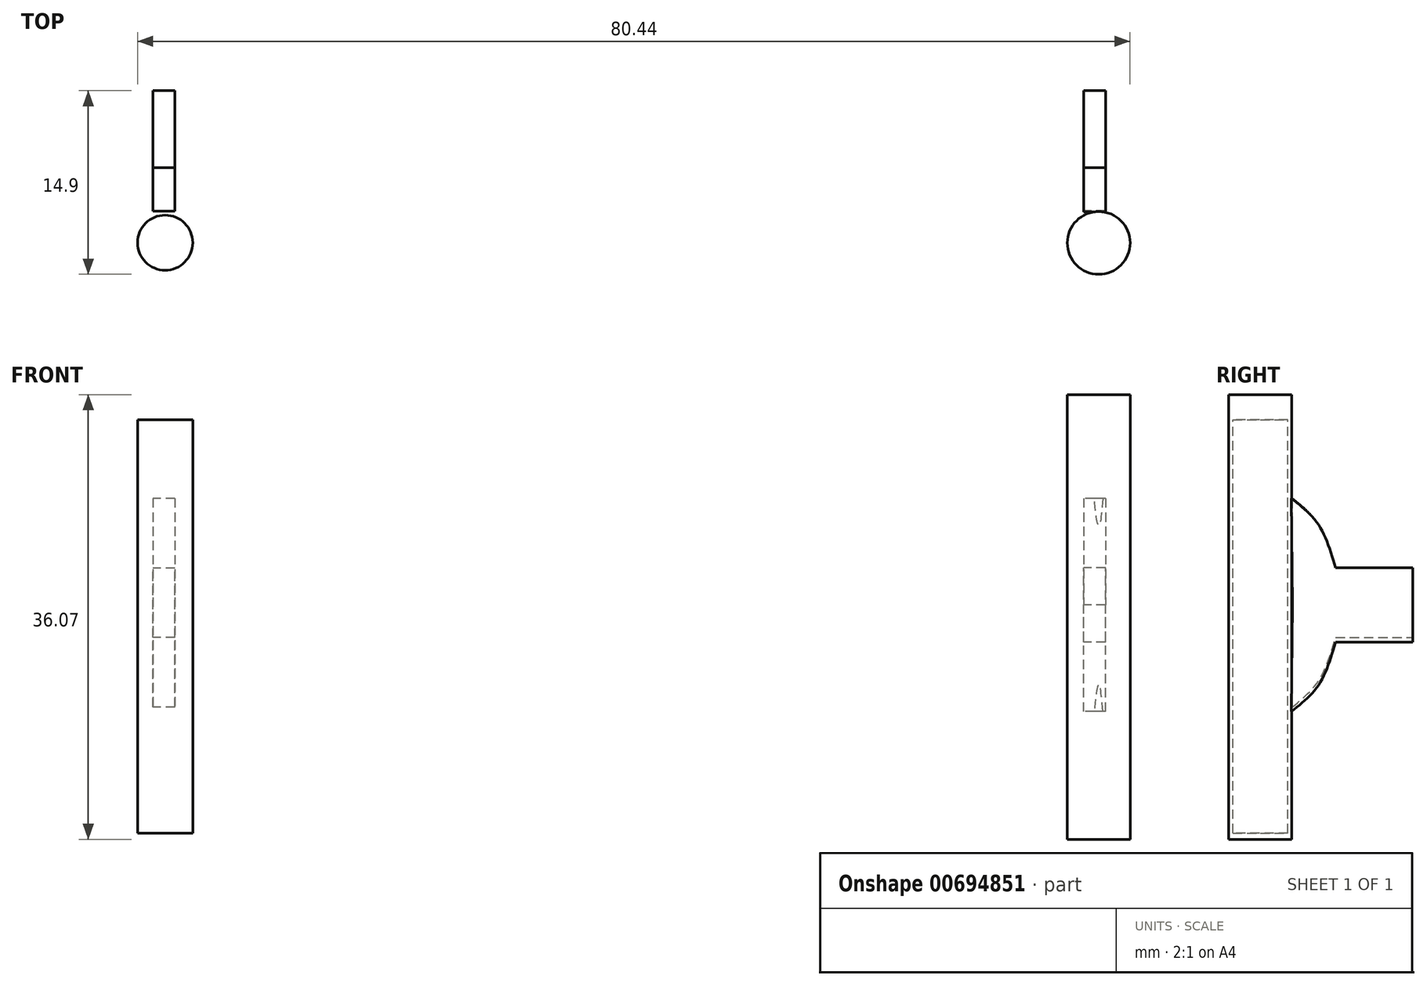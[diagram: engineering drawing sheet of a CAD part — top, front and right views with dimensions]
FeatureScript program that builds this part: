
annotation { "Feature Type Name" : "Feature", "Feature Type Description" : "" }
export const myFeature = defineFeature(function(context is Context, id is Id, definition is map)
    precondition{}
    {
        {
            var Q0;
            Q0=qCreatedBy(makeId("Top.planeOp"),FACE);
            var sketch = newSketch(context, id + "F0", { "sketchPlane" : qUnion([Q0])});
            skLineSegment(sketch, "E0", {"start": v(-51.87, 6.38) * mm, "end": v(46.37, 6.38) * mm});
            skFitSpline(sketch, "E1", {"points": [v(46.37, 6.38) * mm, v(69.04, 11.27) * mm, v(78.15, 20.83) * mm, v(81.04, 14.83) * mm, v(70.82, 4.6) * mm, v(46.37, 0) * mm, v(0, 0) * mm, v(-50.76, 0) * mm, v(-72.1, 6.38) * mm, v(-78.31, 11.94) * mm, v(-78.1, 18.16) * mm, v(-68.54, 12.16) * mm, v(-51.87, 6.38) * mm], "startDerivative": vector(273.4, 3.83) * mm, "endDerivative": vector(210.6, -44.02) * mm});
            skSolve(sketch);
        }
        {
            var Q0;
            Q0=sQuery(id+"F0.wireOp",EDGE,"E0");
            var Q1;
            Q1=sQuery(id+"F0.wireOp",EDGE,"E1");
            extrude(context, id + "F1", {"bodyType" : ToolBodyType.SURFACE, "surfaceEntities" : qUnion([Q0, Q1]), "depth" : 42.42 * mm, "offsetDistance" : 25.4 * mm});
        }
        {
            var Q0;
            Q0=qCreatedBy(makeId("Right.planeOp"),FACE);
            cPlane(context, id + "F2", {"entities" : qUnion([Q0]), "cplaneType" : CPlaneType.OFFSET, "offset" : 37.6 * mm, "oppositeDirection" : true, "width" : 152.4 * mm, "height" : 152.4 * mm});
        }
        {
            var Q0;
            Q0=qCreatedBy(makeId("Right.planeOp"),FACE);
            cPlane(context, id + "F3", {"entities" : qUnion([Q0]), "cplaneType" : CPlaneType.OFFSET, "offset" : 33.27 * mm, "width" : 152.4 * mm, "height" : 152.4 * mm});
        }
        {
            var Q0;
            Q0=qCreatedBy(makeId("Top.planeOp"),FACE);
            cPlane(context, id + "F4", {"entities" : qUnion([Q0]), "cplaneType" : CPlaneType.OFFSET, "offset" : 32 * mm, "width" : 152.4 * mm, "height" : 152.4 * mm});
        }
        {
            var Q0;
            Q0=qCreatedBy(id+"F4.planeOp",FACE);
            var sketch = newSketch(context, id + "F5", { "sketchPlane" : qUnion([Q0])});
            skCircle(sketch, "E2", {"center": v(-32.8, -12.56) * mm, "radius": 5.12 * mm});
            skCircle(sketch, "E3", {"center": v(39.44, -12.56) * mm, "radius": 5.34 * mm});
            skSolve(sketch);
        }
        {
            var Q0;
            Q0=sQuery(id+"F5.wireOp",EDGE,"E2");
            extrude(context, id + "F6", {"bodyType" : ToolBodyType.SURFACE, "surfaceEntities" : qUnion([Q0]), "depth" : 5.6 * mm, "offsetDistance" : 25.4 * mm});
        }
        {
            var Q0;
            Q0=qCreatedBy(id+"F4.planeOp",FACE);
            var sketch = newSketch(context, id + "F7", { "sketchPlane" : qUnion([Q0])});
            skCircle(sketch, "E4", {"center": v(42.77, -12.33) * mm, "radius": 5.23 * mm});
            skSolve(sketch);
        }
        {
            var Q0;
            Q0=sQuery(id+"F7.wireOp",EDGE,"E4");
            extrude(context, id + "F8", {"bodyType" : ToolBodyType.SURFACE, "surfaceEntities" : qUnion([Q0]), "depth" : 5.6 * mm, "offsetDistance" : 25.4 * mm});
        }
        {
            var Q0;
            Q0=qCreatedBy(makeId("Top.planeOp"),FACE);
            var sketch = newSketch(context, id + "F9", { "sketchPlane" : qUnion([Q0])});
            skCircle(sketch, "E5", {"center": v(-32.8, -12.56) * mm, "radius": 5.25 * mm});
            skCircle(sketch, "E6", {"center": v(43, -12.11) * mm, "radius": 5.28 * mm});
            skSolve(sketch);
        }
        {
            var Q0;
            Q0=sQuery(id+"F9.wireOp",EDGE,"E5");
            extrude(context, id + "F10", {"bodyType" : ToolBodyType.SURFACE, "surfaceEntities" : qUnion([Q0]), "depth" : 5.33 * mm, "offsetDistance" : 25.4 * mm});
        }
        {
            var Q0;
            Q0=qCreatedBy(makeId("Top.planeOp"),FACE);
            var sketch = newSketch(context, id + "F11", { "sketchPlane" : qUnion([Q0])});
            skCircle(sketch, "E7", {"center": v(43, -12.33) * mm, "radius": 5.35 * mm});
            skSolve(sketch);
        }
        {
            var Q0;
            Q0=sQuery(id+"F11.wireOp",EDGE,"E7");
            extrude(context, id + "F12", {"bodyType" : ToolBodyType.SURFACE, "surfaceEntities" : qUnion([Q0]), "depth" : 5.6 * mm, "offsetDistance" : 25.4 * mm});
        }
        {
            var Q0;
            Q0=qCreatedBy(makeId("Front.planeOp"),FACE);
            cPlane(context, id + "F13", {"entities" : qUnion([Q0]), "cplaneType" : CPlaneType.OFFSET, "offset" : 11.94 * mm, "width" : 152.4 * mm, "height" : 152.4 * mm});
        }
        {
            var Q0;
            Q0=qCreatedBy(id+"F4.planeOp",FACE);
            cPlane(context, id + "F14", {"entities" : qUnion([Q0]), "cplaneType" : CPlaneType.OFFSET, "offset" : 2.03 * mm, "width" : 152.4 * mm, "height" : 152.4 * mm});
        }
        {
            var Q0;
            Q0=qCreatedBy(id+"F14.planeOp",FACE);
            var sketch = newSketch(context, id + "F15", { "sketchPlane" : qUnion([Q0])});
            skCircle(sketch, "E8", {"center": v(-32.8, -12.33) * mm, "radius": 2.23 * mm});
            skSolve(sketch);
        }
        {
            var Q0;
            Q0 = qSketchRegion(id + "F15", true);
            extrude(context, id + "F16", {"entities" : qUnion([Q0]), "oppositeDirection" : true, "depth" : 33.53 * mm, "offsetDistance" : 25.4 * mm});
        }
        {
            var Q0;
            Q0=qCreatedBy(makeId("Top.planeOp"),FACE);
            var sketch = newSketch(context, id + "F17", { "sketchPlane" : qUnion([Q0])});
            skCircle(sketch, "E9", {"center": v(42.87, -12.35) * mm, "radius": 2.55 * mm});
            skSolve(sketch);
        }
        {
            var Q0;
            Q0 = qSketchRegion(id + "F17", true);
            extrude(context, id + "F18", {"entities" : qUnion([Q0]), "depth" : 36.07 * mm, "offsetDistance" : 25.4 * mm});
        }
        {
            var Q0;
            Q0=qCreatedBy(id+"F2.planeOp",FACE);
            cPlane(context, id + "F19", {"entities" : qUnion([Q0]), "cplaneType" : CPlaneType.OFFSET, "offset" : 3.8 * mm, "width" : 152.4 * mm, "height" : 152.4 * mm});
        }
        {
            var Q0;
            Q0=qCreatedBy(id+"F19.planeOp",FACE);
            var sketch = newSketch(context, id + "F20", { "sketchPlane" : qUnion([Q0])});
            skLineSegment(sketch, "E10", {"start": v(-14.94, 19.18) * mm, "end": v(64.13, 19.18) * mm, "construction": true});
            skFitSpline(sketch, "E11", {"points": [v(-9.77, 27.65) * mm, v(-7.65, 25.53) * mm, v(-6.24, 22) * mm], "startDerivative": vector(4.94, -4) * mm, "endDerivative": vector(2.18, -7.23) * mm});
            skLineSegment(sketch, "E12", {"start": v(-6.24, 22) * mm, "end": v(0, 22) * mm});
            skLineSegment(sketch, "E13", {"start": v(0, 22) * mm, "end": v(0, 19.18) * mm});
            skLineSegment(sketch, "E14.MirrorCS", {"start": v(-6.24, 16.35) * mm, "end": v(0, 16.35) * mm});
            skFitSpline(sketch, "E15.MirrorCS", {"points": [v(-9.77, 10.7) * mm, v(-7.65, 12.83) * mm, v(-6.24, 16.35) * mm], "startDerivative": vector(4.94, 4) * mm, "endDerivative": vector(2.18, 7.23) * mm});
            skLineSegment(sketch, "E16", {"start": v(-9.77, 27.65) * mm, "end": v(-9.77, 10.7) * mm});
            skLineSegment(sketch, "E17", {"start": v(0, 16.35) * mm, "end": v(0, 19.18) * mm});
            skSolve(sketch);
        }
        {
            var Q0;
            Q0 = qSketchRegion(id + "F20", true);
            extrude(context, id + "F21", {"entities" : qUnion([Q0]), "depth" : 1.78 * mm, "offsetDistance" : 25.4 * mm});
        }
        {
            var Q0;
            Q0=qCreatedBy(id+"F3.planeOp",FACE);
            cPlane(context, id + "F22", {"entities" : qUnion([Q0]), "cplaneType" : CPlaneType.OFFSET, "offset" : 8.38 * mm, "width" : 152.4 * mm, "height" : 152.4 * mm});
        }
        {
            var Q0;
            Q0=qCreatedBy(id+"F22.planeOp",FACE);
            var sketch = newSketch(context, id + "F23", { "sketchPlane" : qUnion([Q0])});
            skLineSegment(sketch, "E18", {"start": v(-9.74, 19) * mm, "end": v(20.8, 19) * mm, "construction": true});
            skFitSpline(sketch, "E19", {"points": [v(-9.83, 27.65) * mm, v(-7.65, 25.54) * mm, v(-6.24, 22.02) * mm], "startDerivative": vector(5.1, -3.95) * mm, "endDerivative": vector(2.15, -7.25) * mm});
            skLineSegment(sketch, "E20", {"start": v(-6.24, 22.02) * mm, "end": v(0, 22.02) * mm});
            skLineSegment(sketch, "E21", {"start": v(0, 22.02) * mm, "end": v(0, 19) * mm});
            skLineSegment(sketch, "E22", {"start": v(-9.83, 27.65) * mm, "end": v(-9.74, 19) * mm});
            skLineSegment(sketch, "E23.MirrorCS", {"start": v(-6.24, 16) * mm, "end": v(0, 16) * mm});
            skLineSegment(sketch, "E24.MirrorCS", {"start": v(0, 16) * mm, "end": v(0, 19) * mm});
            skFitSpline(sketch, "E25.MirrorCS", {"points": [v(-9.83, 10.36) * mm, v(-7.65, 12.47) * mm, v(-6.24, 16) * mm], "startDerivative": vector(5.1, 3.95) * mm, "endDerivative": vector(2.15, 7.25) * mm});
            skLineSegment(sketch, "E26.MirrorCS", {"start": v(-9.83, 10.36) * mm, "end": v(-9.74, 19) * mm});
            skSolve(sketch);
        }
        {
            var Q0;
            Q0 = qSketchRegion(id + "F23", true);
            extrude(context, id + "F24", {"entities" : qUnion([Q0]), "operationType" : NewBodyOperationType.ADD, "depth" : 1.78 * mm, "offsetDistance" : 25.4 * mm});
        }
    });
